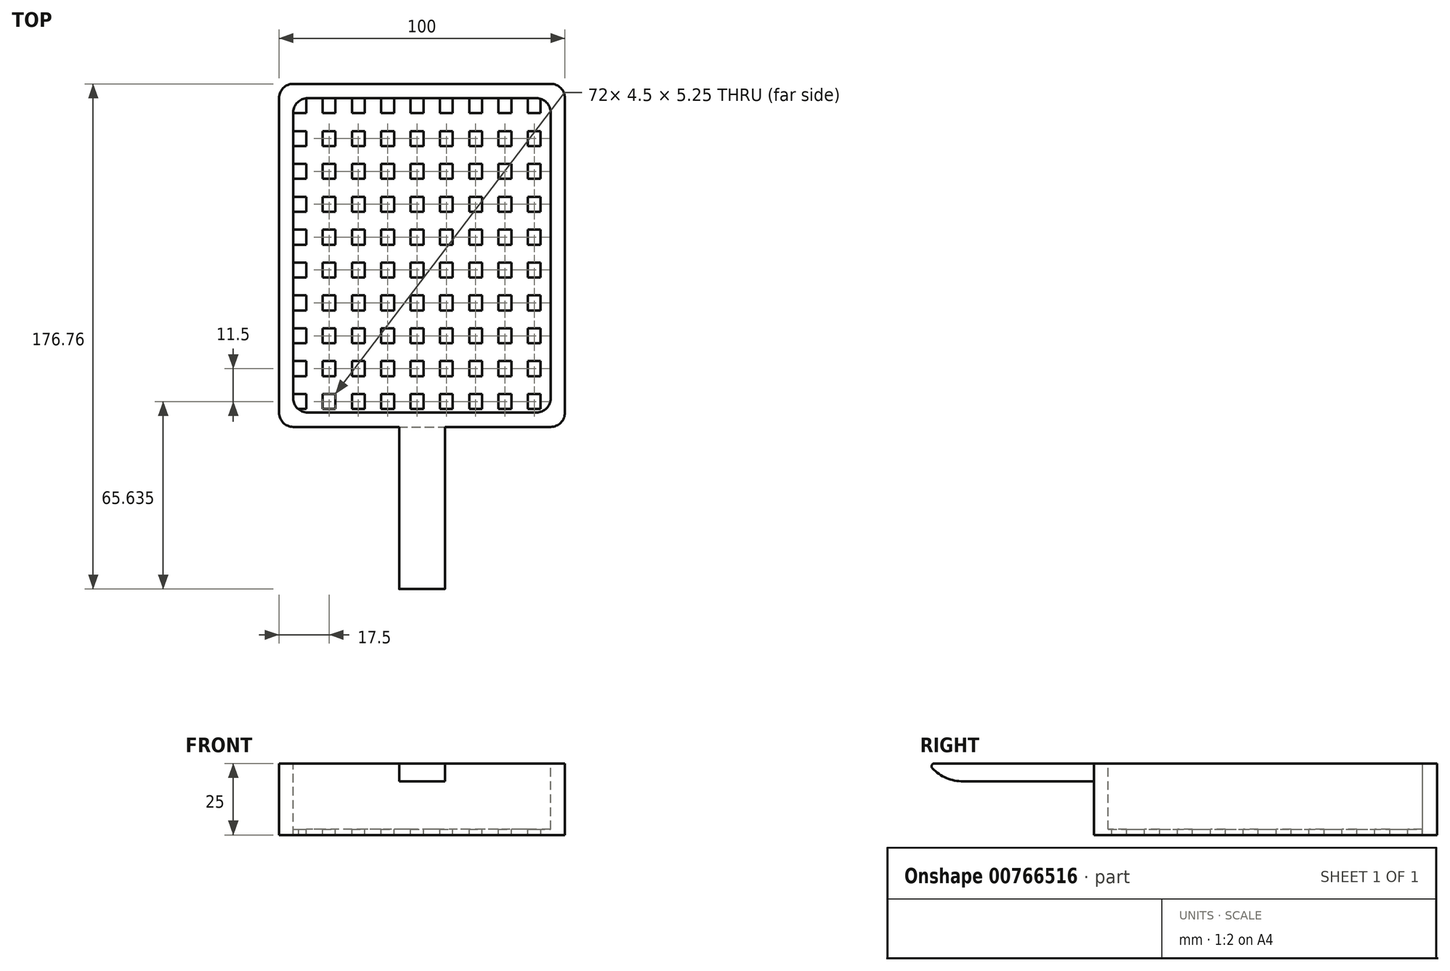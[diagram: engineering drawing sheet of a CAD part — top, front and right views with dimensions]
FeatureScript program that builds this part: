
annotation { "Feature Type Name" : "Feature", "Feature Type Description" : "" }
export const myFeature = defineFeature(function(context is Context, id is Id, definition is map)
    precondition{}
    {
        {
            var Q0;
            Q0=qCreatedBy(makeId("Top.planeOp"),FACE);
            var sketch = newSketch(context, id + "F0", { "sketchPlane" : qUnion([Q0])});
            skLineSegment(sketch, "E0.bottom", {"start": v(-50, 60) * mm, "end": v(50, 60) * mm});
            skLineSegment(sketch, "E0.top", {"start": v(-50, -60) * mm, "end": v(50, -60) * mm});
            skLineSegment(sketch, "E0.left", {"start": v(-50, 60) * mm, "end": v(-50, -60) * mm});
            skLineSegment(sketch, "E0.right", {"start": v(50, 60) * mm, "end": v(50, -60) * mm});
            skPoint(sketch, "E0.middle", {"position": v(0, 0) * mm});
            skSolve(sketch);
        }
        {
            var Q0;
            Q0=makeQuery(id+"F0.imprint","IMPRINT",FACE,{"disambiguationData":[TD([[makeQuery(id+"F0.imprint","IMPRINT",EDGE,{"derivedFrom":sQuery(id+"F0.wireOp",EDGE,"E0.bottom")}),-1.0]])]});
            extrude(context, id + "F1", {"entities" : qUnion([Q0]), "depth" : 25 * mm, "offsetDistance" : 25 * mm});
        }
        {
            var Q0;
            Q0=makeQuery(id+"F1.opExtrude","CAP_FACE",FACE,{"disambiguationData":[OSD([sQuery(id+"F0.wireOp",EDGE,"E0.bottom"),sQuery(id+"F0.wireOp",EDGE,"E0.top"),sQuery(id+"F0.wireOp",EDGE,"E0.left"),sQuery(id+"F0.wireOp",EDGE,"E0.right")])],"isStart":false});
            var sketch = newSketch(context, id + "F2", { "sketchPlane" : qUnion([Q0])});
            skLineSegment(sketch, "E1.bottom", {"start": v(45, -55) * mm, "end": v(-45, -55) * mm});
            skLineSegment(sketch, "E1.top", {"start": v(45, 55) * mm, "end": v(-45, 55) * mm});
            skLineSegment(sketch, "E1.left", {"start": v(45, -55) * mm, "end": v(45, 55) * mm});
            skLineSegment(sketch, "E1.right", {"start": v(-45, -55) * mm, "end": v(-45, 55) * mm});
            skPoint(sketch, "E1.middle", {"position": v(0, 0) * mm});
            skSolve(sketch);
        }
        {
            var Q0;
            Q0=makeQuery(id+"F2.imprint","IMPRINT",FACE,{"disambiguationData":[TD([[makeQuery(id+"F2.imprint","IMPRINT",EDGE,{"derivedFrom":sQuery(id+"F2.wireOp",EDGE,"E1.bottom")}),-1.0]])]});
            extrude(context, id + "F3", {"entities" : qUnion([Q0]), "operationType" : NewBodyOperationType.REMOVE, "oppositeDirection" : true, "depth" : 23 * mm, "offsetDistance" : 25 * mm});
        }
        {
            var Q0;
            Q0=makeQuery(id+"F3.boolean.opBoolean","COPY",FACE,{"derivedFrom":makeQuery(id+"F3.opExtrude","CAP_FACE",FACE,{"disambiguationData":[OSD([sQuery(id+"F2.wireOp",EDGE,"E1.bottom"),sQuery(id+"F2.wireOp",EDGE,"E1.top"),sQuery(id+"F2.wireOp",EDGE,"E1.left"),sQuery(id+"F2.wireOp",EDGE,"E1.right")])],"isStart":false})});
            var sketch = newSketch(context, id + "F4", { "sketchPlane" : qUnion([Q0])});
            skLineSegment(sketch, "E2.bottom", {"start": v(-45, 55) * mm, "end": v(-40.5, 55) * mm});
            skLineSegment(sketch, "E2.top", {"start": v(-45, 49.75) * mm, "end": v(-40.5, 49.75) * mm});
            skLineSegment(sketch, "E2.left", {"start": v(-45, 55) * mm, "end": v(-45, 49.75) * mm});
            skLineSegment(sketch, "E2.right", {"start": v(-40.5, 55) * mm, "end": v(-40.5, 49.75) * mm});
            skLineSegment(sketch, "E3.0.1.0", {"start": v(-40.5, 43.5) * mm, "end": v(-40.5, 38.25) * mm});
            skLineSegment(sketch, "E3.0.1.1", {"start": v(-45, 38.25) * mm, "end": v(-40.5, 38.25) * mm});
            skLineSegment(sketch, "E3.0.1.2", {"start": v(-45, 43.5) * mm, "end": v(-45, 38.25) * mm});
            skLineSegment(sketch, "E3.0.1.3", {"start": v(-45, 43.5) * mm, "end": v(-40.5, 43.5) * mm});
            skLineSegment(sketch, "E3.0.2.0", {"start": v(-40.5, 32) * mm, "end": v(-40.5, 26.75) * mm});
            skLineSegment(sketch, "E3.0.2.1", {"start": v(-45, 26.75) * mm, "end": v(-40.5, 26.75) * mm});
            skLineSegment(sketch, "E3.0.2.2", {"start": v(-45, 32) * mm, "end": v(-45, 26.75) * mm});
            skLineSegment(sketch, "E3.0.2.3", {"start": v(-45, 32) * mm, "end": v(-40.5, 32) * mm});
            skLineSegment(sketch, "E3.0.3.0", {"start": v(-40.5, 20.5) * mm, "end": v(-40.5, 15.25) * mm});
            skLineSegment(sketch, "E3.0.3.1", {"start": v(-45, 15.25) * mm, "end": v(-40.5, 15.25) * mm});
            skLineSegment(sketch, "E3.0.3.2", {"start": v(-45, 20.5) * mm, "end": v(-45, 15.25) * mm});
            skLineSegment(sketch, "E3.0.3.3", {"start": v(-45, 20.5) * mm, "end": v(-40.5, 20.5) * mm});
            skLineSegment(sketch, "E3.0.4.0", {"start": v(-40.5, 9) * mm, "end": v(-40.5, 3.75) * mm});
            skLineSegment(sketch, "E3.0.4.1", {"start": v(-45, 3.75) * mm, "end": v(-40.5, 3.75) * mm});
            skLineSegment(sketch, "E3.0.4.2", {"start": v(-45, 9) * mm, "end": v(-45, 3.75) * mm});
            skLineSegment(sketch, "E3.0.4.3", {"start": v(-45, 9) * mm, "end": v(-40.5, 9) * mm});
            skLineSegment(sketch, "E3.0.5.0", {"start": v(-40.5, -2.5) * mm, "end": v(-40.5, -7.75) * mm});
            skLineSegment(sketch, "E3.0.5.1", {"start": v(-45, -7.75) * mm, "end": v(-40.5, -7.75) * mm});
            skLineSegment(sketch, "E3.0.5.2", {"start": v(-45, -2.5) * mm, "end": v(-45, -7.75) * mm});
            skLineSegment(sketch, "E3.0.5.3", {"start": v(-45, -2.5) * mm, "end": v(-40.5, -2.5) * mm});
            skLineSegment(sketch, "E3.0.6.0", {"start": v(-40.5, -14) * mm, "end": v(-40.5, -19.25) * mm});
            skLineSegment(sketch, "E3.0.6.1", {"start": v(-45, -19.25) * mm, "end": v(-40.5, -19.25) * mm});
            skLineSegment(sketch, "E3.0.6.2", {"start": v(-45, -14) * mm, "end": v(-45, -19.25) * mm});
            skLineSegment(sketch, "E3.0.6.3", {"start": v(-45, -14) * mm, "end": v(-40.5, -14) * mm});
            skLineSegment(sketch, "E3.0.7.0", {"start": v(-40.5, -25.5) * mm, "end": v(-40.5, -30.75) * mm});
            skLineSegment(sketch, "E3.0.7.1", {"start": v(-45, -30.75) * mm, "end": v(-40.5, -30.75) * mm});
            skLineSegment(sketch, "E3.0.7.2", {"start": v(-45, -25.5) * mm, "end": v(-45, -30.75) * mm});
            skLineSegment(sketch, "E3.0.7.3", {"start": v(-45, -25.5) * mm, "end": v(-40.5, -25.5) * mm});
            skLineSegment(sketch, "E3.0.8.0", {"start": v(-40.5, -37) * mm, "end": v(-40.5, -42.25) * mm});
            skLineSegment(sketch, "E3.0.8.1", {"start": v(-45, -42.25) * mm, "end": v(-40.5, -42.25) * mm});
            skLineSegment(sketch, "E3.0.8.2", {"start": v(-45, -37) * mm, "end": v(-45, -42.25) * mm});
            skLineSegment(sketch, "E3.0.8.3", {"start": v(-45, -37) * mm, "end": v(-40.5, -37) * mm});
            skLineSegment(sketch, "E3.0.9.0", {"start": v(-40.5, -48.5) * mm, "end": v(-40.5, -53.75) * mm});
            skLineSegment(sketch, "E3.0.9.1", {"start": v(-45, -53.75) * mm, "end": v(-40.5, -53.75) * mm});
            skLineSegment(sketch, "E3.0.9.2", {"start": v(-45, -48.5) * mm, "end": v(-45, -53.75) * mm});
            skLineSegment(sketch, "E3.0.9.3", {"start": v(-45, -48.5) * mm, "end": v(-40.5, -48.5) * mm});
            skLineSegment(sketch, "E3.1.0.0", {"start": v(-30.25, 55) * mm, "end": v(-30.25, 49.75) * mm});
            skLineSegment(sketch, "E3.1.0.1", {"start": v(-34.75, 49.75) * mm, "end": v(-30.25, 49.75) * mm});
            skLineSegment(sketch, "E3.1.0.2", {"start": v(-34.75, 55) * mm, "end": v(-34.75, 49.75) * mm});
            skLineSegment(sketch, "E3.1.0.3", {"start": v(-34.75, 55) * mm, "end": v(-30.25, 55) * mm});
            skLineSegment(sketch, "E3.1.1.0", {"start": v(-30.25, 43.5) * mm, "end": v(-30.25, 38.25) * mm});
            skLineSegment(sketch, "E3.1.1.1", {"start": v(-34.75, 38.25) * mm, "end": v(-30.25, 38.25) * mm});
            skLineSegment(sketch, "E3.1.1.2", {"start": v(-34.75, 43.5) * mm, "end": v(-34.75, 38.25) * mm});
            skLineSegment(sketch, "E3.1.1.3", {"start": v(-34.75, 43.5) * mm, "end": v(-30.25, 43.5) * mm});
            skLineSegment(sketch, "E3.1.2.0", {"start": v(-30.25, 32) * mm, "end": v(-30.25, 26.75) * mm});
            skLineSegment(sketch, "E3.1.2.1", {"start": v(-34.75, 26.75) * mm, "end": v(-30.25, 26.75) * mm});
            skLineSegment(sketch, "E3.1.2.2", {"start": v(-34.75, 32) * mm, "end": v(-34.75, 26.75) * mm});
            skLineSegment(sketch, "E3.1.2.3", {"start": v(-34.75, 32) * mm, "end": v(-30.25, 32) * mm});
            skLineSegment(sketch, "E3.1.3.0", {"start": v(-30.25, 20.5) * mm, "end": v(-30.25, 15.25) * mm});
            skLineSegment(sketch, "E3.1.3.1", {"start": v(-34.75, 15.25) * mm, "end": v(-30.25, 15.25) * mm});
            skLineSegment(sketch, "E3.1.3.2", {"start": v(-34.75, 20.5) * mm, "end": v(-34.75, 15.25) * mm});
            skLineSegment(sketch, "E3.1.3.3", {"start": v(-34.75, 20.5) * mm, "end": v(-30.25, 20.5) * mm});
            skLineSegment(sketch, "E3.1.4.0", {"start": v(-30.25, 9) * mm, "end": v(-30.25, 3.75) * mm});
            skLineSegment(sketch, "E3.1.4.1", {"start": v(-34.75, 3.75) * mm, "end": v(-30.25, 3.75) * mm});
            skLineSegment(sketch, "E3.1.4.2", {"start": v(-34.75, 9) * mm, "end": v(-34.75, 3.75) * mm});
            skLineSegment(sketch, "E3.1.4.3", {"start": v(-34.75, 9) * mm, "end": v(-30.25, 9) * mm});
            skLineSegment(sketch, "E3.1.5.0", {"start": v(-30.25, -2.5) * mm, "end": v(-30.25, -7.75) * mm});
            skLineSegment(sketch, "E3.1.5.1", {"start": v(-34.75, -7.75) * mm, "end": v(-30.25, -7.75) * mm});
            skLineSegment(sketch, "E3.1.5.2", {"start": v(-34.75, -2.5) * mm, "end": v(-34.75, -7.75) * mm});
            skLineSegment(sketch, "E3.1.5.3", {"start": v(-34.75, -2.5) * mm, "end": v(-30.25, -2.5) * mm});
            skLineSegment(sketch, "E3.1.6.0", {"start": v(-30.25, -14) * mm, "end": v(-30.25, -19.25) * mm});
            skLineSegment(sketch, "E3.1.6.1", {"start": v(-34.75, -19.25) * mm, "end": v(-30.25, -19.25) * mm});
            skLineSegment(sketch, "E3.1.6.2", {"start": v(-34.75, -14) * mm, "end": v(-34.75, -19.25) * mm});
            skLineSegment(sketch, "E3.1.6.3", {"start": v(-34.75, -14) * mm, "end": v(-30.25, -14) * mm});
            skLineSegment(sketch, "E3.1.7.0", {"start": v(-30.25, -25.5) * mm, "end": v(-30.25, -30.75) * mm});
            skLineSegment(sketch, "E3.1.7.1", {"start": v(-34.75, -30.75) * mm, "end": v(-30.25, -30.75) * mm});
            skLineSegment(sketch, "E3.1.7.2", {"start": v(-34.75, -25.5) * mm, "end": v(-34.75, -30.75) * mm});
            skLineSegment(sketch, "E3.1.7.3", {"start": v(-34.75, -25.5) * mm, "end": v(-30.25, -25.5) * mm});
            skLineSegment(sketch, "E3.1.8.0", {"start": v(-30.25, -37) * mm, "end": v(-30.25, -42.25) * mm});
            skLineSegment(sketch, "E3.1.8.1", {"start": v(-34.75, -42.25) * mm, "end": v(-30.25, -42.25) * mm});
            skLineSegment(sketch, "E3.1.8.2", {"start": v(-34.75, -37) * mm, "end": v(-34.75, -42.25) * mm});
            skLineSegment(sketch, "E3.1.8.3", {"start": v(-34.75, -37) * mm, "end": v(-30.25, -37) * mm});
            skLineSegment(sketch, "E3.1.9.0", {"start": v(-30.25, -48.5) * mm, "end": v(-30.25, -53.75) * mm});
            skLineSegment(sketch, "E3.1.9.1", {"start": v(-34.75, -53.75) * mm, "end": v(-30.25, -53.75) * mm});
            skLineSegment(sketch, "E3.1.9.2", {"start": v(-34.75, -48.5) * mm, "end": v(-34.75, -53.75) * mm});
            skLineSegment(sketch, "E3.1.9.3", {"start": v(-34.75, -48.5) * mm, "end": v(-30.25, -48.5) * mm});
            skLineSegment(sketch, "E3.2.0.0", {"start": v(-20, 55) * mm, "end": v(-20, 49.75) * mm});
            skLineSegment(sketch, "E3.2.0.1", {"start": v(-24.5, 49.75) * mm, "end": v(-20, 49.75) * mm});
            skLineSegment(sketch, "E3.2.0.2", {"start": v(-24.5, 55) * mm, "end": v(-24.5, 49.75) * mm});
            skLineSegment(sketch, "E3.2.0.3", {"start": v(-24.5, 55) * mm, "end": v(-20, 55) * mm});
            skLineSegment(sketch, "E3.2.1.0", {"start": v(-20, 43.5) * mm, "end": v(-20, 38.25) * mm});
            skLineSegment(sketch, "E3.2.1.1", {"start": v(-24.5, 38.25) * mm, "end": v(-20, 38.25) * mm});
            skLineSegment(sketch, "E3.2.1.2", {"start": v(-24.5, 43.5) * mm, "end": v(-24.5, 38.25) * mm});
            skLineSegment(sketch, "E3.2.1.3", {"start": v(-24.5, 43.5) * mm, "end": v(-20, 43.5) * mm});
            skLineSegment(sketch, "E3.2.2.0", {"start": v(-20, 32) * mm, "end": v(-20, 26.75) * mm});
            skLineSegment(sketch, "E3.2.2.1", {"start": v(-24.5, 26.75) * mm, "end": v(-20, 26.75) * mm});
            skLineSegment(sketch, "E3.2.2.2", {"start": v(-24.5, 32) * mm, "end": v(-24.5, 26.75) * mm});
            skLineSegment(sketch, "E3.2.2.3", {"start": v(-24.5, 32) * mm, "end": v(-20, 32) * mm});
            skLineSegment(sketch, "E3.2.3.0", {"start": v(-20, 20.5) * mm, "end": v(-20, 15.25) * mm});
            skLineSegment(sketch, "E3.2.3.1", {"start": v(-24.5, 15.25) * mm, "end": v(-20, 15.25) * mm});
            skLineSegment(sketch, "E3.2.3.2", {"start": v(-24.5, 20.5) * mm, "end": v(-24.5, 15.25) * mm});
            skLineSegment(sketch, "E3.2.3.3", {"start": v(-24.5, 20.5) * mm, "end": v(-20, 20.5) * mm});
            skLineSegment(sketch, "E3.2.4.0", {"start": v(-20, 9) * mm, "end": v(-20, 3.75) * mm});
            skLineSegment(sketch, "E3.2.4.1", {"start": v(-24.5, 3.75) * mm, "end": v(-20, 3.75) * mm});
            skLineSegment(sketch, "E3.2.4.2", {"start": v(-24.5, 9) * mm, "end": v(-24.5, 3.75) * mm});
            skLineSegment(sketch, "E3.2.4.3", {"start": v(-24.5, 9) * mm, "end": v(-20, 9) * mm});
            skLineSegment(sketch, "E3.2.5.0", {"start": v(-20, -2.5) * mm, "end": v(-20, -7.75) * mm});
            skLineSegment(sketch, "E3.2.5.1", {"start": v(-24.5, -7.75) * mm, "end": v(-20, -7.75) * mm});
            skLineSegment(sketch, "E3.2.5.2", {"start": v(-24.5, -2.5) * mm, "end": v(-24.5, -7.75) * mm});
            skLineSegment(sketch, "E3.2.5.3", {"start": v(-24.5, -2.5) * mm, "end": v(-20, -2.5) * mm});
            skLineSegment(sketch, "E3.2.6.0", {"start": v(-20, -14) * mm, "end": v(-20, -19.25) * mm});
            skLineSegment(sketch, "E3.2.6.1", {"start": v(-24.5, -19.25) * mm, "end": v(-20, -19.25) * mm});
            skLineSegment(sketch, "E3.2.6.2", {"start": v(-24.5, -14) * mm, "end": v(-24.5, -19.25) * mm});
            skLineSegment(sketch, "E3.2.6.3", {"start": v(-24.5, -14) * mm, "end": v(-20, -14) * mm});
            skLineSegment(sketch, "E3.2.7.0", {"start": v(-20, -25.5) * mm, "end": v(-20, -30.75) * mm});
            skLineSegment(sketch, "E3.2.7.1", {"start": v(-24.5, -30.75) * mm, "end": v(-20, -30.75) * mm});
            skLineSegment(sketch, "E3.2.7.2", {"start": v(-24.5, -25.5) * mm, "end": v(-24.5, -30.75) * mm});
            skLineSegment(sketch, "E3.2.7.3", {"start": v(-24.5, -25.5) * mm, "end": v(-20, -25.5) * mm});
            skLineSegment(sketch, "E3.2.8.0", {"start": v(-20, -37) * mm, "end": v(-20, -42.25) * mm});
            skLineSegment(sketch, "E3.2.8.1", {"start": v(-24.5, -42.25) * mm, "end": v(-20, -42.25) * mm});
            skLineSegment(sketch, "E3.2.8.2", {"start": v(-24.5, -37) * mm, "end": v(-24.5, -42.25) * mm});
            skLineSegment(sketch, "E3.2.8.3", {"start": v(-24.5, -37) * mm, "end": v(-20, -37) * mm});
            skLineSegment(sketch, "E3.2.9.0", {"start": v(-20, -48.5) * mm, "end": v(-20, -53.75) * mm});
            skLineSegment(sketch, "E3.2.9.1", {"start": v(-24.5, -53.75) * mm, "end": v(-20, -53.75) * mm});
            skLineSegment(sketch, "E3.2.9.2", {"start": v(-24.5, -48.5) * mm, "end": v(-24.5, -53.75) * mm});
            skLineSegment(sketch, "E3.2.9.3", {"start": v(-24.5, -48.5) * mm, "end": v(-20, -48.5) * mm});
            skLineSegment(sketch, "E3.3.0.0", {"start": v(-9.75, 55) * mm, "end": v(-9.75, 49.75) * mm});
            skLineSegment(sketch, "E3.3.0.1", {"start": v(-14.25, 49.75) * mm, "end": v(-9.75, 49.75) * mm});
            skLineSegment(sketch, "E3.3.0.2", {"start": v(-14.25, 55) * mm, "end": v(-14.25, 49.75) * mm});
            skLineSegment(sketch, "E3.3.0.3", {"start": v(-14.25, 55) * mm, "end": v(-9.75, 55) * mm});
            skLineSegment(sketch, "E3.3.1.0", {"start": v(-9.75, 43.5) * mm, "end": v(-9.75, 38.25) * mm});
            skLineSegment(sketch, "E3.3.1.1", {"start": v(-14.25, 38.25) * mm, "end": v(-9.75, 38.25) * mm});
            skLineSegment(sketch, "E3.3.1.2", {"start": v(-14.25, 43.5) * mm, "end": v(-14.25, 38.25) * mm});
            skLineSegment(sketch, "E3.3.1.3", {"start": v(-14.25, 43.5) * mm, "end": v(-9.75, 43.5) * mm});
            skLineSegment(sketch, "E3.3.2.0", {"start": v(-9.75, 32) * mm, "end": v(-9.75, 26.75) * mm});
            skLineSegment(sketch, "E3.3.2.1", {"start": v(-14.25, 26.75) * mm, "end": v(-9.75, 26.75) * mm});
            skLineSegment(sketch, "E3.3.2.2", {"start": v(-14.25, 32) * mm, "end": v(-14.25, 26.75) * mm});
            skLineSegment(sketch, "E3.3.2.3", {"start": v(-14.25, 32) * mm, "end": v(-9.75, 32) * mm});
            skLineSegment(sketch, "E3.3.3.0", {"start": v(-9.75, 20.5) * mm, "end": v(-9.75, 15.25) * mm});
            skLineSegment(sketch, "E3.3.3.1", {"start": v(-14.25, 15.25) * mm, "end": v(-9.75, 15.25) * mm});
            skLineSegment(sketch, "E3.3.3.2", {"start": v(-14.25, 20.5) * mm, "end": v(-14.25, 15.25) * mm});
            skLineSegment(sketch, "E3.3.3.3", {"start": v(-14.25, 20.5) * mm, "end": v(-9.75, 20.5) * mm});
            skLineSegment(sketch, "E3.3.4.0", {"start": v(-9.75, 9) * mm, "end": v(-9.75, 3.75) * mm});
            skLineSegment(sketch, "E3.3.4.1", {"start": v(-14.25, 3.75) * mm, "end": v(-9.75, 3.75) * mm});
            skLineSegment(sketch, "E3.3.4.2", {"start": v(-14.25, 9) * mm, "end": v(-14.25, 3.75) * mm});
            skLineSegment(sketch, "E3.3.4.3", {"start": v(-14.25, 9) * mm, "end": v(-9.75, 9) * mm});
            skLineSegment(sketch, "E3.3.5.0", {"start": v(-9.75, -2.5) * mm, "end": v(-9.75, -7.75) * mm});
            skLineSegment(sketch, "E3.3.5.1", {"start": v(-14.25, -7.75) * mm, "end": v(-9.75, -7.75) * mm});
            skLineSegment(sketch, "E3.3.5.2", {"start": v(-14.25, -2.5) * mm, "end": v(-14.25, -7.75) * mm});
            skLineSegment(sketch, "E3.3.5.3", {"start": v(-14.25, -2.5) * mm, "end": v(-9.75, -2.5) * mm});
            skLineSegment(sketch, "E3.3.6.0", {"start": v(-9.75, -14) * mm, "end": v(-9.75, -19.25) * mm});
            skLineSegment(sketch, "E3.3.6.1", {"start": v(-14.25, -19.25) * mm, "end": v(-9.75, -19.25) * mm});
            skLineSegment(sketch, "E3.3.6.2", {"start": v(-14.25, -14) * mm, "end": v(-14.25, -19.25) * mm});
            skLineSegment(sketch, "E3.3.6.3", {"start": v(-14.25, -14) * mm, "end": v(-9.75, -14) * mm});
            skLineSegment(sketch, "E3.3.7.0", {"start": v(-9.75, -25.5) * mm, "end": v(-9.75, -30.75) * mm});
            skLineSegment(sketch, "E3.3.7.1", {"start": v(-14.25, -30.75) * mm, "end": v(-9.75, -30.75) * mm});
            skLineSegment(sketch, "E3.3.7.2", {"start": v(-14.25, -25.5) * mm, "end": v(-14.25, -30.75) * mm});
            skLineSegment(sketch, "E3.3.7.3", {"start": v(-14.25, -25.5) * mm, "end": v(-9.75, -25.5) * mm});
            skLineSegment(sketch, "E3.3.8.0", {"start": v(-9.75, -37) * mm, "end": v(-9.75, -42.25) * mm});
            skLineSegment(sketch, "E3.3.8.1", {"start": v(-14.25, -42.25) * mm, "end": v(-9.75, -42.25) * mm});
            skLineSegment(sketch, "E3.3.8.2", {"start": v(-14.25, -37) * mm, "end": v(-14.25, -42.25) * mm});
            skLineSegment(sketch, "E3.3.8.3", {"start": v(-14.25, -37) * mm, "end": v(-9.75, -37) * mm});
            skLineSegment(sketch, "E3.3.9.0", {"start": v(-9.75, -48.5) * mm, "end": v(-9.75, -53.75) * mm});
            skLineSegment(sketch, "E3.3.9.1", {"start": v(-14.25, -53.75) * mm, "end": v(-9.75, -53.75) * mm});
            skLineSegment(sketch, "E3.3.9.2", {"start": v(-14.25, -48.5) * mm, "end": v(-14.25, -53.75) * mm});
            skLineSegment(sketch, "E3.3.9.3", {"start": v(-14.25, -48.5) * mm, "end": v(-9.75, -48.5) * mm});
            skLineSegment(sketch, "E3.4.0.0", {"start": v(0.5, 55) * mm, "end": v(0.5, 49.75) * mm});
            skLineSegment(sketch, "E3.4.0.1", {"start": v(-4, 49.75) * mm, "end": v(0.5, 49.75) * mm});
            skLineSegment(sketch, "E3.4.0.2", {"start": v(-4, 55) * mm, "end": v(-4, 49.75) * mm});
            skLineSegment(sketch, "E3.4.0.3", {"start": v(-4, 55) * mm, "end": v(0.5, 55) * mm});
            skLineSegment(sketch, "E3.4.1.0", {"start": v(0.5, 43.5) * mm, "end": v(0.5, 38.25) * mm});
            skLineSegment(sketch, "E3.4.1.1", {"start": v(-4, 38.25) * mm, "end": v(0.5, 38.25) * mm});
            skLineSegment(sketch, "E3.4.1.2", {"start": v(-4, 43.5) * mm, "end": v(-4, 38.25) * mm});
            skLineSegment(sketch, "E3.4.1.3", {"start": v(-4, 43.5) * mm, "end": v(0.5, 43.5) * mm});
            skLineSegment(sketch, "E3.4.2.0", {"start": v(0.5, 32) * mm, "end": v(0.5, 26.75) * mm});
            skLineSegment(sketch, "E3.4.2.1", {"start": v(-4, 26.75) * mm, "end": v(0.5, 26.75) * mm});
            skLineSegment(sketch, "E3.4.2.2", {"start": v(-4, 32) * mm, "end": v(-4, 26.75) * mm});
            skLineSegment(sketch, "E3.4.2.3", {"start": v(-4, 32) * mm, "end": v(0.5, 32) * mm});
            skLineSegment(sketch, "E3.4.3.0", {"start": v(0.5, 20.5) * mm, "end": v(0.5, 15.25) * mm});
            skLineSegment(sketch, "E3.4.3.1", {"start": v(-4, 15.25) * mm, "end": v(0.5, 15.25) * mm});
            skLineSegment(sketch, "E3.4.3.2", {"start": v(-4, 20.5) * mm, "end": v(-4, 15.25) * mm});
            skLineSegment(sketch, "E3.4.3.3", {"start": v(-4, 20.5) * mm, "end": v(0.5, 20.5) * mm});
            skLineSegment(sketch, "E3.4.4.0", {"start": v(0.5, 9) * mm, "end": v(0.5, 3.75) * mm});
            skLineSegment(sketch, "E3.4.4.1", {"start": v(-4, 3.75) * mm, "end": v(0.5, 3.75) * mm});
            skLineSegment(sketch, "E3.4.4.2", {"start": v(-4, 9) * mm, "end": v(-4, 3.75) * mm});
            skLineSegment(sketch, "E3.4.4.3", {"start": v(-4, 9) * mm, "end": v(0.5, 9) * mm});
            skLineSegment(sketch, "E3.4.5.0", {"start": v(0.5, -2.5) * mm, "end": v(0.5, -7.75) * mm});
            skLineSegment(sketch, "E3.4.5.1", {"start": v(-4, -7.75) * mm, "end": v(0.5, -7.75) * mm});
            skLineSegment(sketch, "E3.4.5.2", {"start": v(-4, -2.5) * mm, "end": v(-4, -7.75) * mm});
            skLineSegment(sketch, "E3.4.5.3", {"start": v(-4, -2.5) * mm, "end": v(0.5, -2.5) * mm});
            skLineSegment(sketch, "E3.4.6.0", {"start": v(0.5, -14) * mm, "end": v(0.5, -19.25) * mm});
            skLineSegment(sketch, "E3.4.6.1", {"start": v(-4, -19.25) * mm, "end": v(0.5, -19.25) * mm});
            skLineSegment(sketch, "E3.4.6.2", {"start": v(-4, -14) * mm, "end": v(-4, -19.25) * mm});
            skLineSegment(sketch, "E3.4.6.3", {"start": v(-4, -14) * mm, "end": v(0.5, -14) * mm});
            skLineSegment(sketch, "E3.4.7.0", {"start": v(0.5, -25.5) * mm, "end": v(0.5, -30.75) * mm});
            skLineSegment(sketch, "E3.4.7.1", {"start": v(-4, -30.75) * mm, "end": v(0.5, -30.75) * mm});
            skLineSegment(sketch, "E3.4.7.2", {"start": v(-4, -25.5) * mm, "end": v(-4, -30.75) * mm});
            skLineSegment(sketch, "E3.4.7.3", {"start": v(-4, -25.5) * mm, "end": v(0.5, -25.5) * mm});
            skLineSegment(sketch, "E3.4.8.0", {"start": v(0.5, -37) * mm, "end": v(0.5, -42.25) * mm});
            skLineSegment(sketch, "E3.4.8.1", {"start": v(-4, -42.25) * mm, "end": v(0.5, -42.25) * mm});
            skLineSegment(sketch, "E3.4.8.2", {"start": v(-4, -37) * mm, "end": v(-4, -42.25) * mm});
            skLineSegment(sketch, "E3.4.8.3", {"start": v(-4, -37) * mm, "end": v(0.5, -37) * mm});
            skLineSegment(sketch, "E3.4.9.0", {"start": v(0.5, -48.5) * mm, "end": v(0.5, -53.75) * mm});
            skLineSegment(sketch, "E3.4.9.1", {"start": v(-4, -53.75) * mm, "end": v(0.5, -53.75) * mm});
            skLineSegment(sketch, "E3.4.9.2", {"start": v(-4, -48.5) * mm, "end": v(-4, -53.75) * mm});
            skLineSegment(sketch, "E3.4.9.3", {"start": v(-4, -48.5) * mm, "end": v(0.5, -48.5) * mm});
            skLineSegment(sketch, "E3.5.0.0", {"start": v(10.75, 55) * mm, "end": v(10.75, 49.75) * mm});
            skLineSegment(sketch, "E3.5.0.1", {"start": v(6.25, 49.75) * mm, "end": v(10.75, 49.75) * mm});
            skLineSegment(sketch, "E3.5.0.2", {"start": v(6.25, 55) * mm, "end": v(6.25, 49.75) * mm});
            skLineSegment(sketch, "E3.5.0.3", {"start": v(6.25, 55) * mm, "end": v(10.75, 55) * mm});
            skLineSegment(sketch, "E3.5.1.0", {"start": v(10.75, 43.5) * mm, "end": v(10.75, 38.25) * mm});
            skLineSegment(sketch, "E3.5.1.1", {"start": v(6.25, 38.25) * mm, "end": v(10.75, 38.25) * mm});
            skLineSegment(sketch, "E3.5.1.2", {"start": v(6.25, 43.5) * mm, "end": v(6.25, 38.25) * mm});
            skLineSegment(sketch, "E3.5.1.3", {"start": v(6.25, 43.5) * mm, "end": v(10.75, 43.5) * mm});
            skLineSegment(sketch, "E3.5.2.0", {"start": v(10.75, 32) * mm, "end": v(10.75, 26.75) * mm});
            skLineSegment(sketch, "E3.5.2.1", {"start": v(6.25, 26.75) * mm, "end": v(10.75, 26.75) * mm});
            skLineSegment(sketch, "E3.5.2.2", {"start": v(6.25, 32) * mm, "end": v(6.25, 26.75) * mm});
            skLineSegment(sketch, "E3.5.2.3", {"start": v(6.25, 32) * mm, "end": v(10.75, 32) * mm});
            skLineSegment(sketch, "E3.5.3.0", {"start": v(10.75, 20.5) * mm, "end": v(10.75, 15.25) * mm});
            skLineSegment(sketch, "E3.5.3.1", {"start": v(6.25, 15.25) * mm, "end": v(10.75, 15.25) * mm});
            skLineSegment(sketch, "E3.5.3.2", {"start": v(6.25, 20.5) * mm, "end": v(6.25, 15.25) * mm});
            skLineSegment(sketch, "E3.5.3.3", {"start": v(6.25, 20.5) * mm, "end": v(10.75, 20.5) * mm});
            skLineSegment(sketch, "E3.5.4.0", {"start": v(10.75, 9) * mm, "end": v(10.75, 3.75) * mm});
            skLineSegment(sketch, "E3.5.4.1", {"start": v(6.25, 3.75) * mm, "end": v(10.75, 3.75) * mm});
            skLineSegment(sketch, "E3.5.4.2", {"start": v(6.25, 9) * mm, "end": v(6.25, 3.75) * mm});
            skLineSegment(sketch, "E3.5.4.3", {"start": v(6.25, 9) * mm, "end": v(10.75, 9) * mm});
            skLineSegment(sketch, "E3.5.5.0", {"start": v(10.75, -2.5) * mm, "end": v(10.75, -7.75) * mm});
            skLineSegment(sketch, "E3.5.5.1", {"start": v(6.25, -7.75) * mm, "end": v(10.75, -7.75) * mm});
            skLineSegment(sketch, "E3.5.5.2", {"start": v(6.25, -2.5) * mm, "end": v(6.25, -7.75) * mm});
            skLineSegment(sketch, "E3.5.5.3", {"start": v(6.25, -2.5) * mm, "end": v(10.75, -2.5) * mm});
            skLineSegment(sketch, "E3.5.6.0", {"start": v(10.75, -14) * mm, "end": v(10.75, -19.25) * mm});
            skLineSegment(sketch, "E3.5.6.1", {"start": v(6.25, -19.25) * mm, "end": v(10.75, -19.25) * mm});
            skLineSegment(sketch, "E3.5.6.2", {"start": v(6.25, -14) * mm, "end": v(6.25, -19.25) * mm});
            skLineSegment(sketch, "E3.5.6.3", {"start": v(6.25, -14) * mm, "end": v(10.75, -14) * mm});
            skLineSegment(sketch, "E3.5.7.0", {"start": v(10.75, -25.5) * mm, "end": v(10.75, -30.75) * mm});
            skLineSegment(sketch, "E3.5.7.1", {"start": v(6.25, -30.75) * mm, "end": v(10.75, -30.75) * mm});
            skLineSegment(sketch, "E3.5.7.2", {"start": v(6.25, -25.5) * mm, "end": v(6.25, -30.75) * mm});
            skLineSegment(sketch, "E3.5.7.3", {"start": v(6.25, -25.5) * mm, "end": v(10.75, -25.5) * mm});
            skLineSegment(sketch, "E3.5.8.0", {"start": v(10.75, -37) * mm, "end": v(10.75, -42.25) * mm});
            skLineSegment(sketch, "E3.5.8.1", {"start": v(6.25, -42.25) * mm, "end": v(10.75, -42.25) * mm});
            skLineSegment(sketch, "E3.5.8.2", {"start": v(6.25, -37) * mm, "end": v(6.25, -42.25) * mm});
            skLineSegment(sketch, "E3.5.8.3", {"start": v(6.25, -37) * mm, "end": v(10.75, -37) * mm});
            skLineSegment(sketch, "E3.5.9.0", {"start": v(10.75, -48.5) * mm, "end": v(10.75, -53.75) * mm});
            skLineSegment(sketch, "E3.5.9.1", {"start": v(6.25, -53.75) * mm, "end": v(10.75, -53.75) * mm});
            skLineSegment(sketch, "E3.5.9.2", {"start": v(6.25, -48.5) * mm, "end": v(6.25, -53.75) * mm});
            skLineSegment(sketch, "E3.5.9.3", {"start": v(6.25, -48.5) * mm, "end": v(10.75, -48.5) * mm});
            skLineSegment(sketch, "E3.6.0.0", {"start": v(21, 55) * mm, "end": v(21, 49.75) * mm});
            skLineSegment(sketch, "E3.6.0.1", {"start": v(16.5, 49.75) * mm, "end": v(21, 49.75) * mm});
            skLineSegment(sketch, "E3.6.0.2", {"start": v(16.5, 55) * mm, "end": v(16.5, 49.75) * mm});
            skLineSegment(sketch, "E3.6.0.3", {"start": v(16.5, 55) * mm, "end": v(21, 55) * mm});
            skLineSegment(sketch, "E3.6.1.0", {"start": v(21, 43.5) * mm, "end": v(21, 38.25) * mm});
            skLineSegment(sketch, "E3.6.1.1", {"start": v(16.5, 38.25) * mm, "end": v(21, 38.25) * mm});
            skLineSegment(sketch, "E3.6.1.2", {"start": v(16.5, 43.5) * mm, "end": v(16.5, 38.25) * mm});
            skLineSegment(sketch, "E3.6.1.3", {"start": v(16.5, 43.5) * mm, "end": v(21, 43.5) * mm});
            skLineSegment(sketch, "E3.6.2.0", {"start": v(21, 32) * mm, "end": v(21, 26.75) * mm});
            skLineSegment(sketch, "E3.6.2.1", {"start": v(16.5, 26.75) * mm, "end": v(21, 26.75) * mm});
            skLineSegment(sketch, "E3.6.2.2", {"start": v(16.5, 32) * mm, "end": v(16.5, 26.75) * mm});
            skLineSegment(sketch, "E3.6.2.3", {"start": v(16.5, 32) * mm, "end": v(21, 32) * mm});
            skLineSegment(sketch, "E3.6.3.0", {"start": v(21, 20.5) * mm, "end": v(21, 15.25) * mm});
            skLineSegment(sketch, "E3.6.3.1", {"start": v(16.5, 15.25) * mm, "end": v(21, 15.25) * mm});
            skLineSegment(sketch, "E3.6.3.2", {"start": v(16.5, 20.5) * mm, "end": v(16.5, 15.25) * mm});
            skLineSegment(sketch, "E3.6.3.3", {"start": v(16.5, 20.5) * mm, "end": v(21, 20.5) * mm});
            skLineSegment(sketch, "E3.6.4.0", {"start": v(21, 9) * mm, "end": v(21, 3.75) * mm});
            skLineSegment(sketch, "E3.6.4.1", {"start": v(16.5, 3.75) * mm, "end": v(21, 3.75) * mm});
            skLineSegment(sketch, "E3.6.4.2", {"start": v(16.5, 9) * mm, "end": v(16.5, 3.75) * mm});
            skLineSegment(sketch, "E3.6.4.3", {"start": v(16.5, 9) * mm, "end": v(21, 9) * mm});
            skLineSegment(sketch, "E3.6.5.0", {"start": v(21, -2.5) * mm, "end": v(21, -7.75) * mm});
            skLineSegment(sketch, "E3.6.5.1", {"start": v(16.5, -7.75) * mm, "end": v(21, -7.75) * mm});
            skLineSegment(sketch, "E3.6.5.2", {"start": v(16.5, -2.5) * mm, "end": v(16.5, -7.75) * mm});
            skLineSegment(sketch, "E3.6.5.3", {"start": v(16.5, -2.5) * mm, "end": v(21, -2.5) * mm});
            skLineSegment(sketch, "E3.6.6.0", {"start": v(21, -14) * mm, "end": v(21, -19.25) * mm});
            skLineSegment(sketch, "E3.6.6.1", {"start": v(16.5, -19.25) * mm, "end": v(21, -19.25) * mm});
            skLineSegment(sketch, "E3.6.6.2", {"start": v(16.5, -14) * mm, "end": v(16.5, -19.25) * mm});
            skLineSegment(sketch, "E3.6.6.3", {"start": v(16.5, -14) * mm, "end": v(21, -14) * mm});
            skLineSegment(sketch, "E3.6.7.0", {"start": v(21, -25.5) * mm, "end": v(21, -30.75) * mm});
            skLineSegment(sketch, "E3.6.7.1", {"start": v(16.5, -30.75) * mm, "end": v(21, -30.75) * mm});
            skLineSegment(sketch, "E3.6.7.2", {"start": v(16.5, -25.5) * mm, "end": v(16.5, -30.75) * mm});
            skLineSegment(sketch, "E3.6.7.3", {"start": v(16.5, -25.5) * mm, "end": v(21, -25.5) * mm});
            skLineSegment(sketch, "E3.6.8.0", {"start": v(21, -37) * mm, "end": v(21, -42.25) * mm});
            skLineSegment(sketch, "E3.6.8.1", {"start": v(16.5, -42.25) * mm, "end": v(21, -42.25) * mm});
            skLineSegment(sketch, "E3.6.8.2", {"start": v(16.5, -37) * mm, "end": v(16.5, -42.25) * mm});
            skLineSegment(sketch, "E3.6.8.3", {"start": v(16.5, -37) * mm, "end": v(21, -37) * mm});
            skLineSegment(sketch, "E3.6.9.0", {"start": v(21, -48.5) * mm, "end": v(21, -53.75) * mm});
            skLineSegment(sketch, "E3.6.9.1", {"start": v(16.5, -53.75) * mm, "end": v(21, -53.75) * mm});
            skLineSegment(sketch, "E3.6.9.2", {"start": v(16.5, -48.5) * mm, "end": v(16.5, -53.75) * mm});
            skLineSegment(sketch, "E3.6.9.3", {"start": v(16.5, -48.5) * mm, "end": v(21, -48.5) * mm});
            skLineSegment(sketch, "E3.7.0.0", {"start": v(31.25, 55) * mm, "end": v(31.25, 49.75) * mm});
            skLineSegment(sketch, "E3.7.0.1", {"start": v(26.75, 49.75) * mm, "end": v(31.25, 49.75) * mm});
            skLineSegment(sketch, "E3.7.0.2", {"start": v(26.75, 55) * mm, "end": v(26.75, 49.75) * mm});
            skLineSegment(sketch, "E3.7.0.3", {"start": v(26.75, 55) * mm, "end": v(31.25, 55) * mm});
            skLineSegment(sketch, "E3.7.1.0", {"start": v(31.25, 43.5) * mm, "end": v(31.25, 38.25) * mm});
            skLineSegment(sketch, "E3.7.1.1", {"start": v(26.75, 38.25) * mm, "end": v(31.25, 38.25) * mm});
            skLineSegment(sketch, "E3.7.1.2", {"start": v(26.75, 43.5) * mm, "end": v(26.75, 38.25) * mm});
            skLineSegment(sketch, "E3.7.1.3", {"start": v(26.75, 43.5) * mm, "end": v(31.25, 43.5) * mm});
            skLineSegment(sketch, "E3.7.2.0", {"start": v(31.25, 32) * mm, "end": v(31.25, 26.75) * mm});
            skLineSegment(sketch, "E3.7.2.1", {"start": v(26.75, 26.75) * mm, "end": v(31.25, 26.75) * mm});
            skLineSegment(sketch, "E3.7.2.2", {"start": v(26.75, 32) * mm, "end": v(26.75, 26.75) * mm});
            skLineSegment(sketch, "E3.7.2.3", {"start": v(26.75, 32) * mm, "end": v(31.25, 32) * mm});
            skLineSegment(sketch, "E3.7.3.0", {"start": v(31.25, 20.5) * mm, "end": v(31.25, 15.25) * mm});
            skLineSegment(sketch, "E3.7.3.1", {"start": v(26.75, 15.25) * mm, "end": v(31.25, 15.25) * mm});
            skLineSegment(sketch, "E3.7.3.2", {"start": v(26.75, 20.5) * mm, "end": v(26.75, 15.25) * mm});
            skLineSegment(sketch, "E3.7.3.3", {"start": v(26.75, 20.5) * mm, "end": v(31.25, 20.5) * mm});
            skLineSegment(sketch, "E3.7.4.0", {"start": v(31.25, 9) * mm, "end": v(31.25, 3.75) * mm});
            skLineSegment(sketch, "E3.7.4.1", {"start": v(26.75, 3.75) * mm, "end": v(31.25, 3.75) * mm});
            skLineSegment(sketch, "E3.7.4.2", {"start": v(26.75, 9) * mm, "end": v(26.75, 3.75) * mm});
            skLineSegment(sketch, "E3.7.4.3", {"start": v(26.75, 9) * mm, "end": v(31.25, 9) * mm});
            skLineSegment(sketch, "E3.7.5.0", {"start": v(31.25, -2.5) * mm, "end": v(31.25, -7.75) * mm});
            skLineSegment(sketch, "E3.7.5.1", {"start": v(26.75, -7.75) * mm, "end": v(31.25, -7.75) * mm});
            skLineSegment(sketch, "E3.7.5.2", {"start": v(26.75, -2.5) * mm, "end": v(26.75, -7.75) * mm});
            skLineSegment(sketch, "E3.7.5.3", {"start": v(26.75, -2.5) * mm, "end": v(31.25, -2.5) * mm});
            skLineSegment(sketch, "E3.7.6.0", {"start": v(31.25, -14) * mm, "end": v(31.25, -19.25) * mm});
            skLineSegment(sketch, "E3.7.6.1", {"start": v(26.75, -19.25) * mm, "end": v(31.25, -19.25) * mm});
            skLineSegment(sketch, "E3.7.6.2", {"start": v(26.75, -14) * mm, "end": v(26.75, -19.25) * mm});
            skLineSegment(sketch, "E3.7.6.3", {"start": v(26.75, -14) * mm, "end": v(31.25, -14) * mm});
            skLineSegment(sketch, "E3.7.7.0", {"start": v(31.25, -25.5) * mm, "end": v(31.25, -30.75) * mm});
            skLineSegment(sketch, "E3.7.7.1", {"start": v(26.75, -30.75) * mm, "end": v(31.25, -30.75) * mm});
            skLineSegment(sketch, "E3.7.7.2", {"start": v(26.75, -25.5) * mm, "end": v(26.75, -30.75) * mm});
            skLineSegment(sketch, "E3.7.7.3", {"start": v(26.75, -25.5) * mm, "end": v(31.25, -25.5) * mm});
            skLineSegment(sketch, "E3.7.8.0", {"start": v(31.25, -37) * mm, "end": v(31.25, -42.25) * mm});
            skLineSegment(sketch, "E3.7.8.1", {"start": v(26.75, -42.25) * mm, "end": v(31.25, -42.25) * mm});
            skLineSegment(sketch, "E3.7.8.2", {"start": v(26.75, -37) * mm, "end": v(26.75, -42.25) * mm});
            skLineSegment(sketch, "E3.7.8.3", {"start": v(26.75, -37) * mm, "end": v(31.25, -37) * mm});
            skLineSegment(sketch, "E3.7.9.0", {"start": v(31.25, -48.5) * mm, "end": v(31.25, -53.75) * mm});
            skLineSegment(sketch, "E3.7.9.1", {"start": v(26.75, -53.75) * mm, "end": v(31.25, -53.75) * mm});
            skLineSegment(sketch, "E3.7.9.2", {"start": v(26.75, -48.5) * mm, "end": v(26.75, -53.75) * mm});
            skLineSegment(sketch, "E3.7.9.3", {"start": v(26.75, -48.5) * mm, "end": v(31.25, -48.5) * mm});
            skLineSegment(sketch, "E3.8.0.0", {"start": v(41.5, 55) * mm, "end": v(41.5, 49.75) * mm});
            skLineSegment(sketch, "E3.8.0.1", {"start": v(37, 49.75) * mm, "end": v(41.5, 49.75) * mm});
            skLineSegment(sketch, "E3.8.0.2", {"start": v(37, 55) * mm, "end": v(37, 49.75) * mm});
            skLineSegment(sketch, "E3.8.0.3", {"start": v(37, 55) * mm, "end": v(41.5, 55) * mm});
            skLineSegment(sketch, "E3.8.1.0", {"start": v(41.5, 43.5) * mm, "end": v(41.5, 38.25) * mm});
            skLineSegment(sketch, "E3.8.1.1", {"start": v(37, 38.25) * mm, "end": v(41.5, 38.25) * mm});
            skLineSegment(sketch, "E3.8.1.2", {"start": v(37, 43.5) * mm, "end": v(37, 38.25) * mm});
            skLineSegment(sketch, "E3.8.1.3", {"start": v(37, 43.5) * mm, "end": v(41.5, 43.5) * mm});
            skLineSegment(sketch, "E3.8.2.0", {"start": v(41.5, 32) * mm, "end": v(41.5, 26.75) * mm});
            skLineSegment(sketch, "E3.8.2.1", {"start": v(37, 26.75) * mm, "end": v(41.5, 26.75) * mm});
            skLineSegment(sketch, "E3.8.2.2", {"start": v(37, 32) * mm, "end": v(37, 26.75) * mm});
            skLineSegment(sketch, "E3.8.2.3", {"start": v(37, 32) * mm, "end": v(41.5, 32) * mm});
            skLineSegment(sketch, "E3.8.3.0", {"start": v(41.5, 20.5) * mm, "end": v(41.5, 15.25) * mm});
            skLineSegment(sketch, "E3.8.3.1", {"start": v(37, 15.25) * mm, "end": v(41.5, 15.25) * mm});
            skLineSegment(sketch, "E3.8.3.2", {"start": v(37, 20.5) * mm, "end": v(37, 15.25) * mm});
            skLineSegment(sketch, "E3.8.3.3", {"start": v(37, 20.5) * mm, "end": v(41.5, 20.5) * mm});
            skLineSegment(sketch, "E3.8.4.0", {"start": v(41.5, 9) * mm, "end": v(41.5, 3.75) * mm});
            skLineSegment(sketch, "E3.8.4.1", {"start": v(37, 3.75) * mm, "end": v(41.5, 3.75) * mm});
            skLineSegment(sketch, "E3.8.4.2", {"start": v(37, 9) * mm, "end": v(37, 3.75) * mm});
            skLineSegment(sketch, "E3.8.4.3", {"start": v(37, 9) * mm, "end": v(41.5, 9) * mm});
            skLineSegment(sketch, "E3.8.5.0", {"start": v(41.5, -2.5) * mm, "end": v(41.5, -7.75) * mm});
            skLineSegment(sketch, "E3.8.5.1", {"start": v(37, -7.75) * mm, "end": v(41.5, -7.75) * mm});
            skLineSegment(sketch, "E3.8.5.2", {"start": v(37, -2.5) * mm, "end": v(37, -7.75) * mm});
            skLineSegment(sketch, "E3.8.5.3", {"start": v(37, -2.5) * mm, "end": v(41.5, -2.5) * mm});
            skLineSegment(sketch, "E3.8.6.0", {"start": v(41.5, -14) * mm, "end": v(41.5, -19.25) * mm});
            skLineSegment(sketch, "E3.8.6.1", {"start": v(37, -19.25) * mm, "end": v(41.5, -19.25) * mm});
            skLineSegment(sketch, "E3.8.6.2", {"start": v(37, -14) * mm, "end": v(37, -19.25) * mm});
            skLineSegment(sketch, "E3.8.6.3", {"start": v(37, -14) * mm, "end": v(41.5, -14) * mm});
            skLineSegment(sketch, "E3.8.7.0", {"start": v(41.5, -25.5) * mm, "end": v(41.5, -30.75) * mm});
            skLineSegment(sketch, "E3.8.7.1", {"start": v(37, -30.75) * mm, "end": v(41.5, -30.75) * mm});
            skLineSegment(sketch, "E3.8.7.2", {"start": v(37, -25.5) * mm, "end": v(37, -30.75) * mm});
            skLineSegment(sketch, "E3.8.7.3", {"start": v(37, -25.5) * mm, "end": v(41.5, -25.5) * mm});
            skLineSegment(sketch, "E3.8.8.0", {"start": v(41.5, -37) * mm, "end": v(41.5, -42.25) * mm});
            skLineSegment(sketch, "E3.8.8.1", {"start": v(37, -42.25) * mm, "end": v(41.5, -42.25) * mm});
            skLineSegment(sketch, "E3.8.8.2", {"start": v(37, -37) * mm, "end": v(37, -42.25) * mm});
            skLineSegment(sketch, "E3.8.8.3", {"start": v(37, -37) * mm, "end": v(41.5, -37) * mm});
            skLineSegment(sketch, "E3.8.9.0", {"start": v(41.5, -48.5) * mm, "end": v(41.5, -53.75) * mm});
            skLineSegment(sketch, "E3.8.9.1", {"start": v(37, -53.75) * mm, "end": v(41.5, -53.75) * mm});
            skLineSegment(sketch, "E3.8.9.2", {"start": v(37, -48.5) * mm, "end": v(37, -53.75) * mm});
            skLineSegment(sketch, "E3.8.9.3", {"start": v(37, -48.5) * mm, "end": v(41.5, -48.5) * mm});
            skLineSegment(sketch, "E3.direction1", {"start": v(-40.5, 49.75) * mm, "end": v(-30.25, 49.75) * mm, "construction": true});
            skLineSegment(sketch, "E3.direction2", {"start": v(-40.5, 49.75) * mm, "end": v(-40.5, 38.25) * mm, "construction": true});
            skSolve(sketch);
        }
        {
            var Q0;
            Q0 = qSketchRegion(id + "F4", true);
            extrude(context, id + "F5", {"entities" : qUnion([Q0]), "operationType" : NewBodyOperationType.REMOVE, "oppositeDirection" : true, "depth" : 25 * mm, "offsetDistance" : 25 * mm});
        }
        {
            var Q0;
            Q0=makeQuery(id+"F3.boolean.opBoolean","COPY",EDGE,{"derivedFrom":makeQuery(id+"F3.opExtrude","SWEPT_EDGE",EDGE,{"disambiguationData":[OSD([sQuery(id+"F2.wireOp",EDGE,"E1.bottom"),sQuery(id+"F2.wireOp",EDGE,"E1.right")])]})});
            var Q1;
            Q1=makeQuery(id+"F5.boolean.opBoolean","MERGE",EDGE,{"derivedFrom":[makeQuery(id+"F3.boolean.opBoolean","COPY",EDGE,{"derivedFrom":makeQuery(id+"F3.opExtrude","SWEPT_EDGE",EDGE,{"disambiguationData":[OSD([sQuery(id+"F2.wireOp",EDGE,"E1.top"),sQuery(id+"F2.wireOp",EDGE,"E1.right")])]})}),makeQuery(id+"F5.opExtrude","SWEPT_EDGE",EDGE,{"disambiguationData":[OSD([sQuery(id+"F4.wireOp",EDGE,"E2.bottom"),sQuery(id+"F4.wireOp",EDGE,"E2.left")])]})]});
            var Q2;
            Q2=makeQuery(id+"F1.opExtrude","SWEPT_EDGE",EDGE,{"disambiguationData":[OSD([sQuery(id+"F0.wireOp",EDGE,"E0.top"),sQuery(id+"F0.wireOp",EDGE,"E0.right")])]});
            var Q3;
            Q3=makeQuery(id+"F1.opExtrude","SWEPT_EDGE",EDGE,{"disambiguationData":[OSD([sQuery(id+"F0.wireOp",EDGE,"E0.top"),sQuery(id+"F0.wireOp",EDGE,"E0.left")])]});
            var Q4;
            Q4=makeQuery(id+"F3.boolean.opBoolean","COPY",EDGE,{"derivedFrom":makeQuery(id+"F3.opExtrude","SWEPT_EDGE",EDGE,{"disambiguationData":[OSD([sQuery(id+"F2.wireOp",EDGE,"E1.bottom"),sQuery(id+"F2.wireOp",EDGE,"E1.left")])]})});
            var Q5;
            Q5=makeQuery(id+"F3.boolean.opBoolean","COPY",EDGE,{"derivedFrom":makeQuery(id+"F3.opExtrude","SWEPT_EDGE",EDGE,{"disambiguationData":[OSD([sQuery(id+"F2.wireOp",EDGE,"E1.top"),sQuery(id+"F2.wireOp",EDGE,"E1.left")])]})});
            var Q6;
            Q6=makeQuery(id+"F1.opExtrude","SWEPT_EDGE",EDGE,{"disambiguationData":[OSD([sQuery(id+"F0.wireOp",EDGE,"E0.bottom"),sQuery(id+"F0.wireOp",EDGE,"E0.left")])]});
            var Q7;
            Q7=makeQuery(id+"F1.opExtrude","SWEPT_EDGE",EDGE,{"disambiguationData":[OSD([sQuery(id+"F0.wireOp",EDGE,"E0.bottom"),sQuery(id+"F0.wireOp",EDGE,"E0.right")])]});
            fillet(context, id + "F6", {"entities" : qUnion([Q0, Q1, Q2, Q3, Q4, Q5, Q6, Q7]), "radius" : 5 * mm, "tangentPropagation" : true, "allowEdgeOverflow" : false});
        }
        {
            var Q0;
            Q0=makeQuery(id+"F1.opExtrude","SWEPT_FACE",FACE,{"disambiguationData":[OSD([sQuery(id+"F0.wireOp",EDGE,"E0.top")])]});
            var sketch = newSketch(context, id + "F7", { "sketchPlane" : qUnion([Q0])});
            skLineSegment(sketch, "E4", {"start": v(0, 0) * mm, "end": v(0, 25) * mm, "construction": true});
            skLineSegment(sketch, "E5", {"start": v(0, 12.5) * mm, "end": v(0, 25) * mm, "construction": true});
            skLineSegment(sketch, "E6", {"start": v(0, 18.75) * mm, "end": v(-8, 18.75) * mm, "construction": true});
            skLineSegment(sketch, "E7", {"start": v(-8, 18.75) * mm, "end": v(-8, 25) * mm, "construction": true});
            skLineSegment(sketch, "E8.bottom", {"start": v(-8, 25) * mm, "end": v(8, 25) * mm});
            skLineSegment(sketch, "E8.top", {"start": v(-8, 18.75) * mm, "end": v(8, 18.75) * mm});
            skLineSegment(sketch, "E8.left", {"start": v(-8, 25) * mm, "end": v(-8, 18.75) * mm});
            skLineSegment(sketch, "E8.right", {"start": v(8, 25) * mm, "end": v(8, 18.75) * mm});
            skSolve(sketch);
        }
        {
            var Q0;
            Q0=makeQuery(id+"F7.imprint","IMPRINT",FACE,{"disambiguationData":[TD([[makeQuery(id+"F7.imprint","IMPRINT",EDGE,{"derivedFrom":sQuery(id+"F7.wireOp",EDGE,"E8.bottom")}),-1.0]])]});
            extrude(context, id + "F8", {"entities" : qUnion([Q0]), "operationType" : NewBodyOperationType.ADD, "depth" : 57.9 * mm, "offsetDistance" : 25 * mm});
        }
        {
            var Q0;
            Q0=makeQuery(id+"F8.opExtrude","CAP_EDGE",EDGE,{"disambiguationData":[OSD([sQuery(id+"F7.wireOp",EDGE,"E8.top")])],"isStart":false});
            fillet(context, id + "F9", {"entities" : qUnion([Q0]), "radius" : 15 * mm, "tangentPropagation" : true, "allowEdgeOverflow" : false});
        }
        {
            var Q0;
            Q0=makeQuery(id+"F9.opFillet","BLEND_EDGE",EDGE,{"blendedFrom":[makeQuery(id+"F8.opExtrude","CAP_EDGE",EDGE,{"disambiguationData":[OSD([sQuery(id+"F7.wireOp",EDGE,"E8.top")])],"isStart":false}),makeQuery(id+"F8.boolean.opBoolean","MERGE",FACE,{"derivedFrom":[makeQuery(id+"F1.opExtrude","CAP_FACE",FACE,{"disambiguationData":[OSD([sQuery(id+"F0.wireOp",EDGE,"E0.bottom"),sQuery(id+"F0.wireOp",EDGE,"E0.top"),sQuery(id+"F0.wireOp",EDGE,"E0.left"),sQuery(id+"F0.wireOp",EDGE,"E0.right")])],"isStart":false}),makeQuery(id+"F8.opExtrude","SWEPT_FACE",FACE,{"disambiguationData":[OSD([sQuery(id+"F7.wireOp",EDGE,"E8.bottom")])]})]})],"blendedInto":[makeQuery(id+"F8.boolean.opBoolean","MERGE",FACE,{"derivedFrom":[makeQuery(id+"F1.opExtrude","CAP_FACE",FACE,{"disambiguationData":[OSD([sQuery(id+"F0.wireOp",EDGE,"E0.bottom"),sQuery(id+"F0.wireOp",EDGE,"E0.top"),sQuery(id+"F0.wireOp",EDGE,"E0.left"),sQuery(id+"F0.wireOp",EDGE,"E0.right")])],"isStart":false}),makeQuery(id+"F8.opExtrude","SWEPT_FACE",FACE,{"disambiguationData":[OSD([sQuery(id+"F7.wireOp",EDGE,"E8.bottom")])]})]})]});
            fillet(context, id + "F10", {"entities" : qUnion([Q0]), "radius" : 1 * mm, "tangentPropagation" : true, "allowEdgeOverflow" : false});
        }
    });
